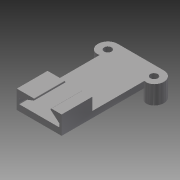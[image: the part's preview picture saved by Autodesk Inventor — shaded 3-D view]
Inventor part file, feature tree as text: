
AUTODESK INVENTOR PART (.ipt)
format: ipt  version: 2015 (Build 190159000, 159)  size: 189,440 bytes
history: native  units: in
note: dims shown in document units (in); Inventor stores cm internally (conversion verified against a paired STEP export)
features: reference x7, extrude x5, sketch x5, projected_geometry x4, fillet x3
ambient origin geometry x8: Origin, YZ Plane, XZ Plane, XY Plane, X Axis, Y Axis, Z Axis, Center Point
bodies: Solid1 (feature_tree)
feature tree (24):
  extrude  "Extrusion1"  Depth=0.728in
  extrude  "Extrusion2"  Depth=0.1in TaperAngle=0.0deg
  fillet  "Fillet1"  Radius=1.33in
  extrude  "Extrusion3"  Depth=0.1in
  fillet  "Fillet2"  Radius=0.015in
  extrude  "Extrusion4"  Depth=0.2in TaperAngle=0.0deg
  extrude  "Extrusion5"  Depth=0.125in
  fillet  "Fillet3"  Radius=0.01in
  sketch  "Sketch1"  dims[d0=0.728in d2=0.12in]
  sketch  "Sketch3"  dims[d4=0.025in d7=0.1in d8=0.0in d12=1.33in]
  reference  "Reference1"
  reference  "Reference2"
  sketch  "Sketch4"  dims[d13=0.75in d14=0.1in d15=0.015in]
  projected_geometry  "Projected Loop2"
  projected_geometry  "Projected Loop3"
  reference  "Reference3"
  reference  "Reference4"
  reference  "Reference5"
  reference  "Reference6"
  reference  "Reference7"
  sketch  "Sketch5"  dims[d16=0.5in d17=0.2in d18=0.0in]
  projected_geometry  "Projected Loop4"
  sketch  "Sketch6"  dims[d19=0.015in d20=0.01in d21=0.01in d22=0.01in d23=0.01in d24=0.2in d25=0.0in d26=0.015in d27=0.2in d28=0.0in d29=0.55in d30=1.0in d31=0.0in d32=0.125in]
  projected_geometry  "Projected Loop5"
